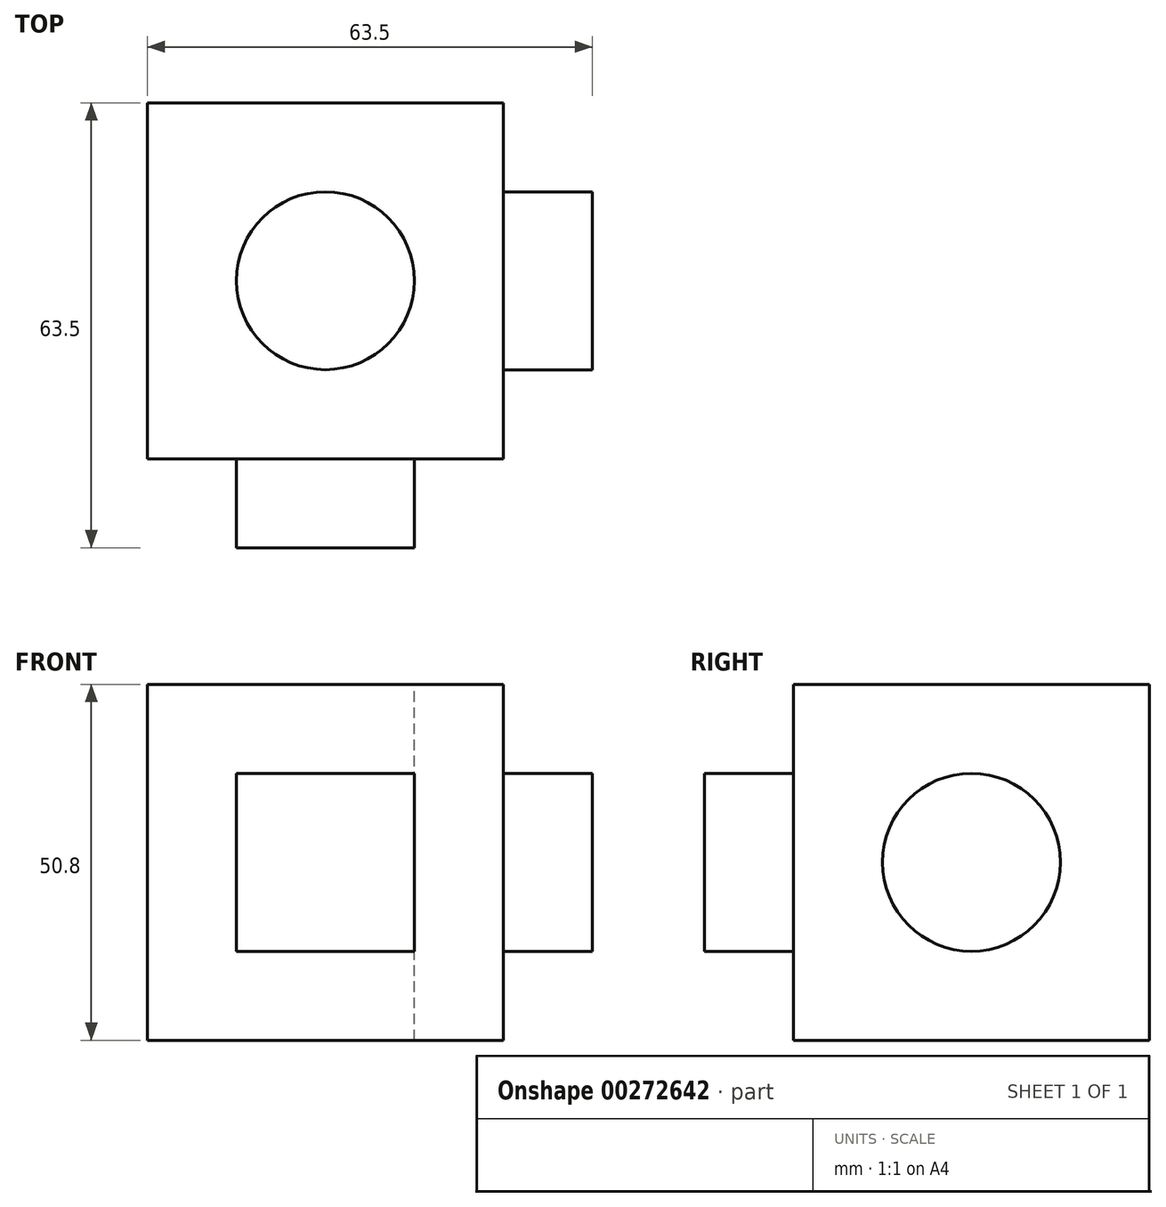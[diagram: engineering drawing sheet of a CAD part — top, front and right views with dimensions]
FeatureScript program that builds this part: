
annotation { "Feature Type Name" : "Feature", "Feature Type Description" : "" }
export const myFeature = defineFeature(function(context is Context, id is Id, definition is map)
    precondition{}
    {
        {
            var Q0;
            Q0=qCreatedBy(makeId("Front.planeOp"),FACE);
            var sketch = newSketch(context, id + "F0", { "sketchPlane" : qUnion([Q0])});
            skLineSegment(sketch, "E0.bottom", {"start": v(0, 0) * mm, "end": v(50.8, 0) * mm});
            skLineSegment(sketch, "E0.top", {"start": v(0, -50.8) * mm, "end": v(50.8, -50.8) * mm});
            skLineSegment(sketch, "E0.left", {"start": v(0, 0) * mm, "end": v(0, -50.8) * mm});
            skLineSegment(sketch, "E0.right", {"start": v(50.8, 0) * mm, "end": v(50.8, -50.8) * mm});
            skSolve(sketch);
        }
        {
            var Q0;
            Q0 = qSketchRegion(id + "F0", true);
            extrude(context, id + "F1", {"entities" : qUnion([Q0]), "depth" : 50.8 * mm});
        }
        {
            var Q0;
            Q0=makeQuery(id+"F1.opExtrude","CAP_FACE",FACE,{"disambiguationData":[OSD([sQuery(id+"F0.wireOp",EDGE,"E0.bottom"),sQuery(id+"F0.wireOp",EDGE,"E0.top"),sQuery(id+"F0.wireOp",EDGE,"E0.left"),sQuery(id+"F0.wireOp",EDGE,"E0.right")])],"isStart":false});
            var sketch = newSketch(context, id + "F2", { "sketchPlane" : qUnion([Q0])});
            skCircle(sketch, "E1", {"center": v(25.4, -25.4) * mm, "radius": 12.7 * mm});
            skSolve(sketch);
        }
        {
            var Q0;
            Q0=makeQuery(id+"F1.opExtrude","SWEPT_FACE",FACE,{"disambiguationData":[OSD([sQuery(id+"F0.wireOp",EDGE,"E0.right")])]});
            var sketch = newSketch(context, id + "F3", { "sketchPlane" : qUnion([Q0])});
            skCircle(sketch, "E2", {"center": v(-25.4, -25.4) * mm, "radius": 12.7 * mm});
            skSolve(sketch);
        }
        {
            var Q0;
            Q0 = qSketchRegion(id + "F3", true);
            extrude(context, id + "F4", {"entities" : qUnion([Q0]), "operationType" : NewBodyOperationType.ADD, "depth" : 12.7 * mm});
        }
        {
            var Q0;
            Q0=makeQuery(id+"F1.opExtrude","SWEPT_FACE",FACE,{"disambiguationData":[OSD([sQuery(id+"F0.wireOp",EDGE,"E0.bottom")])]});
            var sketch = newSketch(context, id + "F5", { "sketchPlane" : qUnion([Q0])});
            skCircle(sketch, "E3", {"center": v(25.4, -25.4) * mm, "radius": 12.7 * mm});
            skSolve(sketch);
        }
        {
            var Q0;
            Q0 = qSketchRegion(id + "F5", true);
            extrude(context, id + "F6", {"entities" : qUnion([Q0]), "operationType" : NewBodyOperationType.REMOVE, "oppositeDirection" : true, "depth" : 50.8 * mm});
        }
        {
            var Q0;
            Q0=makeQuery(id+"F2.imprint","IMPRINT",FACE,{"disambiguationData":[TD([[makeQuery(id+"F2.imprint","IMPRINT",EDGE,{"derivedFrom":sQuery(id+"F2.wireOp",EDGE,"E1")}),1.0]])]});
            var sketch = newSketch(context, id + "F7", { "sketchPlane" : qUnion([Q0])});
            skLineSegment(sketch, "E4.bottom", {"start": v(38.1, -38.1) * mm, "end": v(12.7, -38.1) * mm});
            skLineSegment(sketch, "E4.top", {"start": v(38.1, -12.7) * mm, "end": v(12.7, -12.7) * mm});
            skLineSegment(sketch, "E4.left", {"start": v(38.1, -38.1) * mm, "end": v(38.1, -12.7) * mm});
            skLineSegment(sketch, "E4.right", {"start": v(12.7, -38.1) * mm, "end": v(12.7, -12.7) * mm});
            skPoint(sketch, "E4.middle", {"position": v(25.4, -25.4) * mm});
            skSolve(sketch);
        }
        {
            var Q0;
            Q0 = qSketchRegion(id + "F7", true);
            extrude(context, id + "F8", {"entities" : qUnion([Q0]), "operationType" : NewBodyOperationType.ADD, "depth" : 12.7 * mm});
        }
    });
